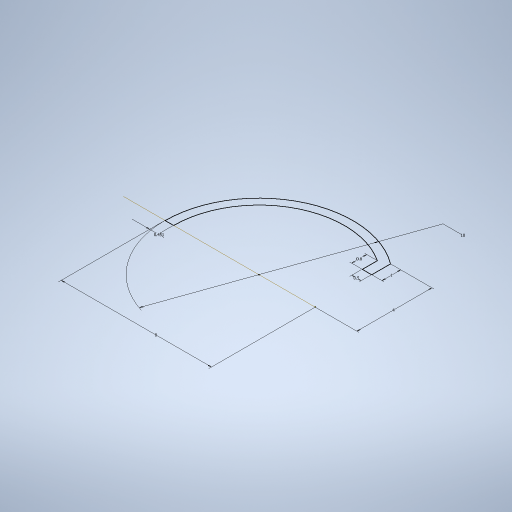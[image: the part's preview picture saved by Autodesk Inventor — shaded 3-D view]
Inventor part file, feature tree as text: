
AUTODESK INVENTOR PART (.ipt)
format: ipt  version: 2024.2 (Build 282272000, 272)  size: 238,080 bytes
history: native  units: mm
features: sketch x1
ambient origin geometry x8: Origin, YZ Plane, XZ Plane, XY Plane, X Axis, Y Axis, Z Axis, Center Point
feature tree (1):
  sketch  "Sketch1"  dims[d1=10.0mm d5=4.0mm d6=1.0mm d7=0.5mm d8=0.8mm d9=8.0mm d10=0.451374mm]
